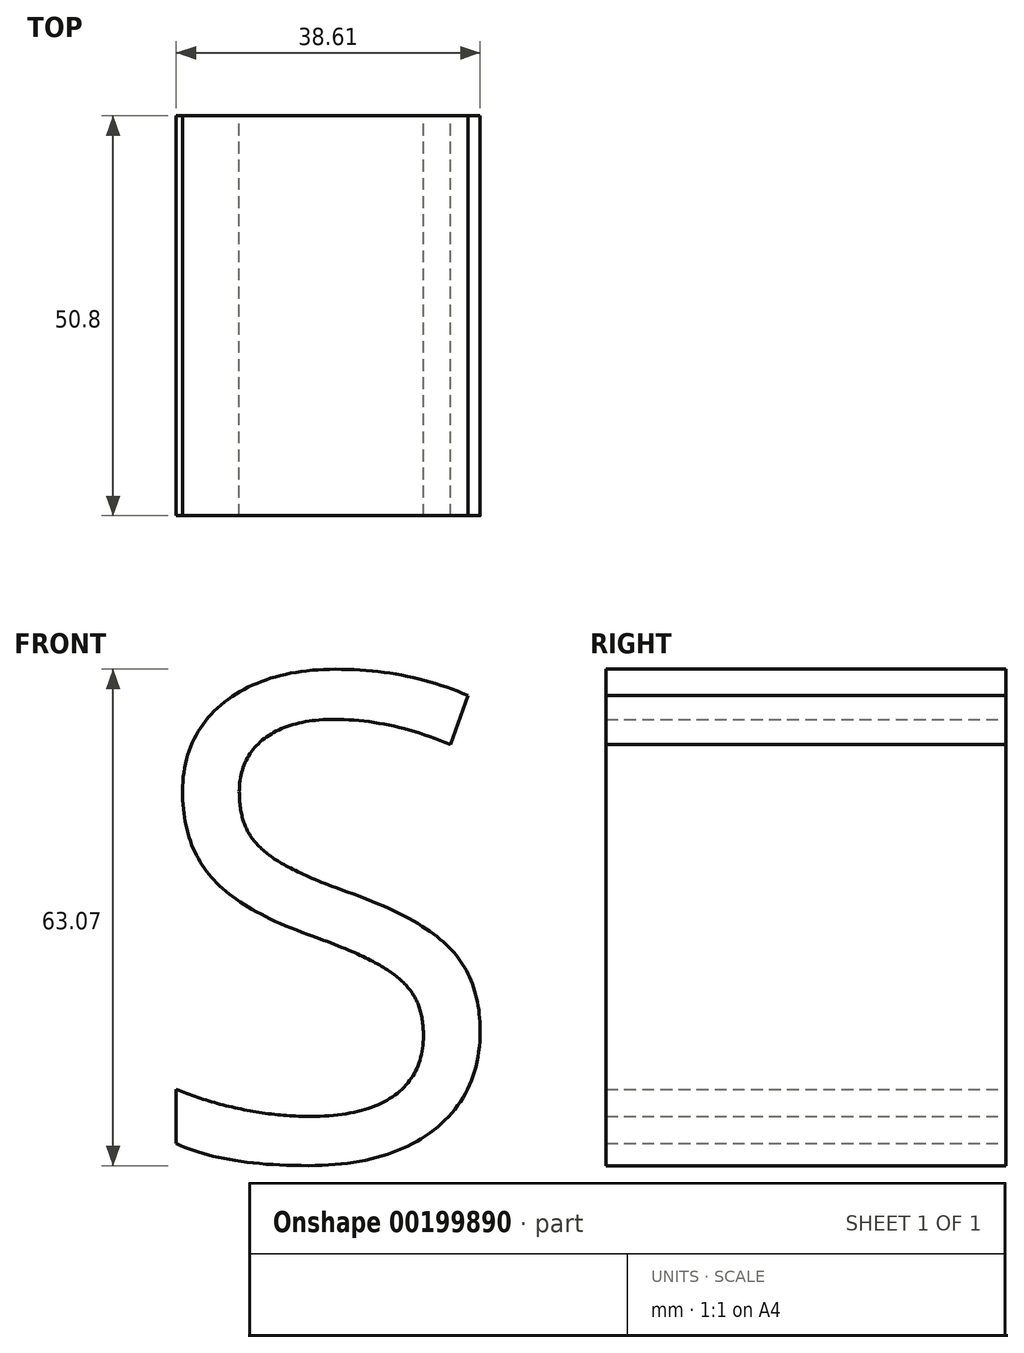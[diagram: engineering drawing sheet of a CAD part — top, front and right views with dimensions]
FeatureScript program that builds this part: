
annotation { "Feature Type Name" : "Feature", "Feature Type Description" : "" }
export const myFeature = defineFeature(function(context is Context, id is Id, definition is map)
    precondition{}
    {
        {
            var Q0;
            Q0=qCreatedBy(makeId("Front.planeOp"), FACE);
            var sketch = newSketch(context, id + "F0", { "sketchPlane" : qUnion([Q0])});
            skText(sketch, "E0", { "text": "S", "fontName": "OpenSans-Regular.ttf"});
            const initialGuessF0  = {"E0": [-0.03404, -0.02832, 1, 0, 0.06187]};
            skSetInitialGuess(sketch, initialGuessF0);
            skSolve(sketch);
        }
        {
            var Q0;
            Q0 = qSketchRegion(id + "F0", true);
            extrude(context, id + "F1", {"entities" : qUnion([Q0]), "domain" : OperationDomain.MODEL, "flatOperationType" : FlatOperationType.REMOVE, "depth" : 50.8 * mm, "offsetDistance" : 25.4 * mm});
        }
    });
